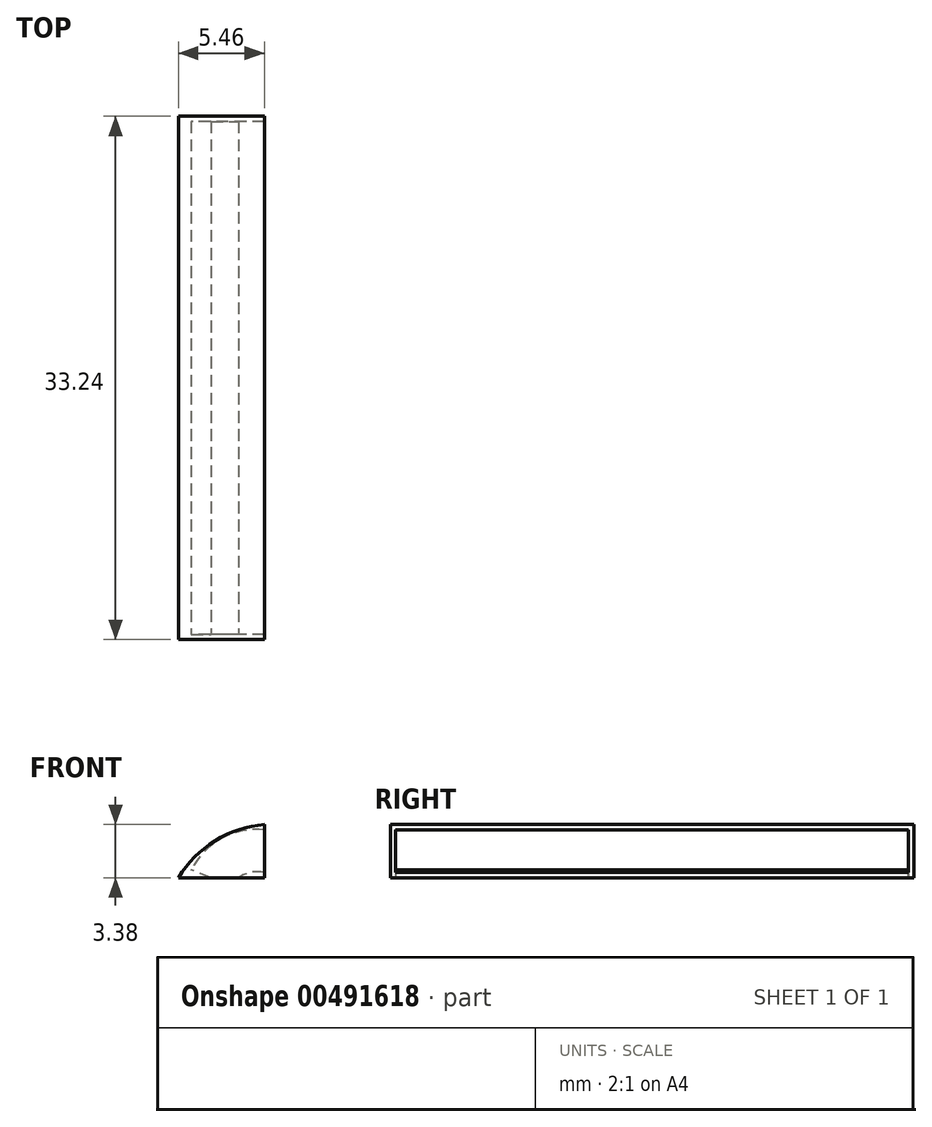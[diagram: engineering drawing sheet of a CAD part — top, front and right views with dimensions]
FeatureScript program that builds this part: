
annotation { "Feature Type Name" : "Feature", "Feature Type Description" : "" }
export const myFeature = defineFeature(function(context is Context, id is Id, definition is map)
    precondition{}
    {
        {
            var Q0;
            Q0=qCreatedBy(makeId("Front.planeOp"),FACE);
            var sketch = newSketch(context, id + "F0", { "sketchPlane" : qUnion([Q0])});
            skLineSegment(sketch, "E0", {"start": v(0, 0) * mm, "end": v(5.46, 0) * mm});
            skLineSegment(sketch, "E1", {"start": v(5.46, 0) * mm, "end": v(5.46, 3.38) * mm});
            skArc(sketch, "E2", {"start": v(5.46, 3.38) * mm, "mid": v(2.32, 2.35) * mm, "end": v(0, 0) * mm});
            skArc(sketch, "E3", {"start": v(5.46, 1.69) * mm, "mid": v(3.86, 1.23) * mm, "end": v(2.73, 0) * mm});
            skSolve(sketch);
        }
        {
            var Q0;
            {var subQ3=sQuery(id+"F0.wireOp",EDGE,"E3");Q0=makeQuery(id+"F0.imprint","IMPRINT",FACE,{"disambiguationData":[TD([[makeQuery(id+"F0.imprint","IMPRINT",EDGE,{"derivedFrom":subQ3}),1.0]])]});}
            var Q1;
            {var subQ0=sQuery(id+"F0.wireOp",EDGE,"E2");Q1=makeQuery(id+"F0.imprint","IMPRINT",FACE,{"disambiguationData":[TD([[makeQuery(id+"F0.imprint","IMPRINT",EDGE,{"derivedFrom":subQ0}),1.0]])]});}
            extrude(context, id + "F1", {"entities" : qUnion([Q0, Q1]), "oppositeDirection" : true, "depth" : 33.24 * mm});
        }
        {
            var Q0;
            Q0=makeQuery(id+"F1.opExtrude","SWEPT_FACE",FACE,{"disambiguationData":[OSD([sQuery(id+"F0.wireOp",EDGE,"E1")])]});
            var sketch = newSketch(context, id + "F2", { "sketchPlane" : qUnion([Q0])});
            skLineSegment(sketch, "E4.0", {"start": v(0.33, 3.05) * mm, "end": v(0.33, 0.33) * mm});
            skLineSegment(sketch, "E4.1", {"start": v(32.91, 3.05) * mm, "end": v(0.33, 3.05) * mm});
            skLineSegment(sketch, "E4.2", {"start": v(32.91, 0.33) * mm, "end": v(32.91, 3.05) * mm});
            skLineSegment(sketch, "E4.3", {"start": v(0.33, 0.33) * mm, "end": v(32.91, 0.33) * mm});
            skSolve(sketch);
        }
        {
            var Q0;
            Q0=makeQuery(id+"F1.opExtrude","CAP_FACE",FACE,{"disambiguationData":[OSD([sQuery(id+"F0.wireOp",EDGE,"E0"),sQuery(id+"F0.wireOp",EDGE,"E1"),sQuery(id+"F0.wireOp",EDGE,"E2")])],"isStart":true});
            var sketch = newSketch(context, id + "F3", { "sketchPlane" : qUnion([Q0])});
            skArc(sketch, "E5", {"start": v(5.46, 1.69) * mm, "mid": v(3.5, 1.37) * mm, "end": v(2.07, 0) * mm});
            skSolve(sketch);
        }
        {
            var Q0;
            Q0=makeQuery(id+"F2.imprint","IMPRINT",FACE,{"disambiguationData":[TD([[makeQuery(id+"F2.imprint","IMPRINT",EDGE,{"derivedFrom":sQuery(id+"F2.wireOp",EDGE,"E4.0")}),1.0]])]});
            var Q1;
            Q1=sQuery(id+"F3.wireOp",EDGE,"E5");
            sweep(context, id + "F4", {"operationType" : NewBodyOperationType.REMOVE, "profiles" : qUnion([Q0]), "path" : qUnion([Q1])});
        }
    });
